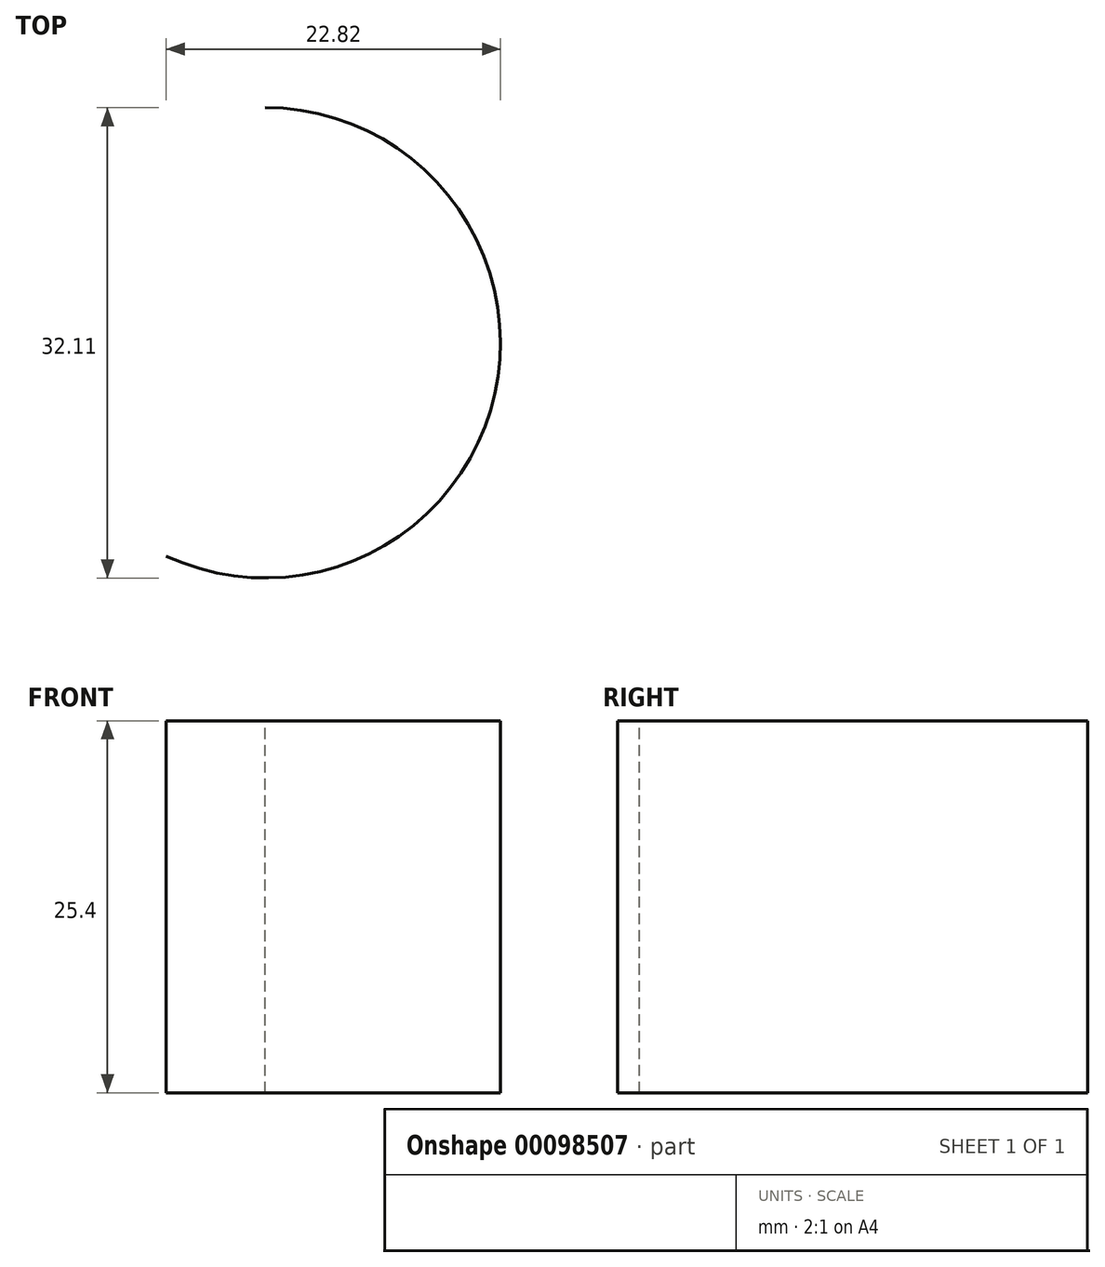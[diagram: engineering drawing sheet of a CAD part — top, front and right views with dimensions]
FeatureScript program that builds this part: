
annotation { "Feature Type Name" : "Feature", "Feature Type Description" : "" }
export const myFeature = defineFeature(function(context is Context, id is Id, definition is map)
    precondition{}
    {
        {
            var Q0;
            Q0=qCreatedBy(makeId("Top.planeOp"),FACE);
            var sketch = newSketch(context, id + "F0", { "sketchPlane" : qUnion([Q0])});
            skLineSegment(sketch, "E0", {"start": v(-23.71, 20.45) * mm, "end": v(-23.71, -27.17) * mm});
            skLineSegment(sketch, "E1", {"start": v(-23.71, 20.45) * mm, "end": v(-56.02, 20.45) * mm});
            skLineSegment(sketch, "E2", {"start": v(-23.71, 12.6) * mm, "end": v(-56.02, 12.6) * mm});
            skLineSegment(sketch, "E3", {"start": v(-56.02, 20.45) * mm, "end": v(-56.02, 12.6) * mm});
            skLineSegment(sketch, "E4", {"start": v(-23.71, -17.46) * mm, "end": v(-55.64, -17.46) * mm});
            skLineSegment(sketch, "E5", {"start": v(-55.64, -17.46) * mm, "end": v(-55.64, -25.3) * mm});
            skLineSegment(sketch, "E6", {"start": v(-55.64, -25.3) * mm, "end": v(-23.71, -27.17) * mm});
            skLineSegment(sketch, "E7", {"start": v(-23.71, 20.45) * mm, "end": v(-16.24, 20.45) * mm});
            skLineSegment(sketch, "E8", {"start": v(-16.24, 20.45) * mm, "end": v(-16.24, -26.05) * mm});
            skLineSegment(sketch, "E9", {"start": v(-16.24, -26.05) * mm, "end": v(-23.71, -27.17) * mm});
            skLineSegment(sketch, "E10", {"start": v(-16.24, -26.05) * mm, "end": v(17.37, -26.05) * mm});
            skArc(sketch, "E11", {"start": v(0, 4.57) * mm, "mid": v(15.68, -14.95) * mm, "end": v(-6.76, -26.05) * mm});
            skSolve(sketch);
        }
        {
            var Q0;
            Q0=sQuery(id+"F0.wireOp",EDGE,"E11");
            extrude(context, id + "F1", {"bodyType" : ToolBodyType.SURFACE, "surfaceEntities" : qUnion([Q0]), "depth" : 25.4 * mm});
        }
    });
